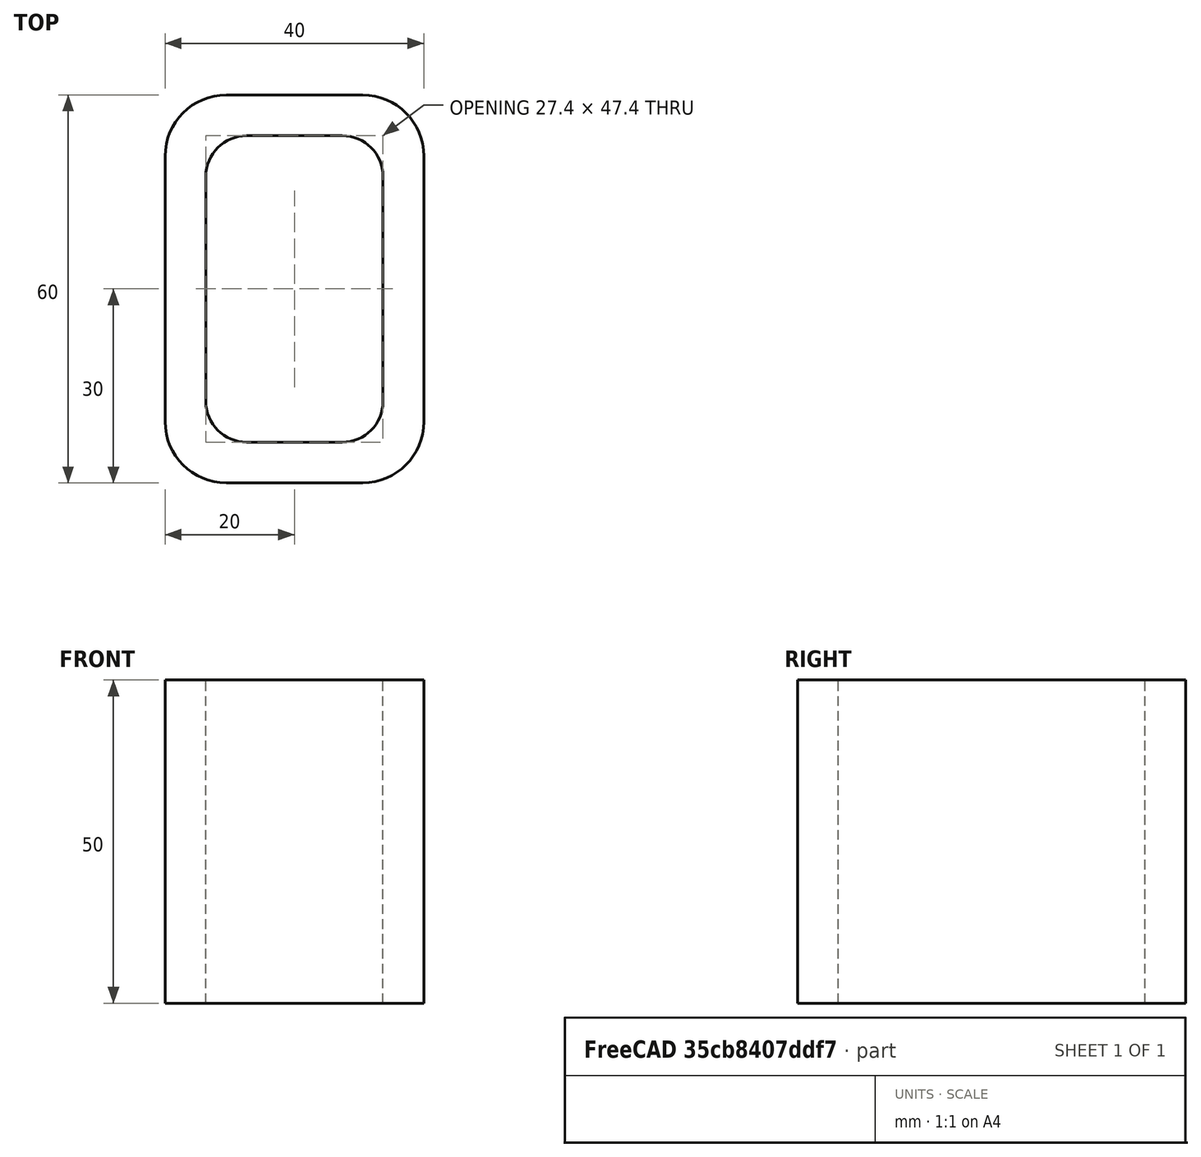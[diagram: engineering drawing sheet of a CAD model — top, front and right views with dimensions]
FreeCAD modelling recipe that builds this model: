
FCSTD DOCUMENT  (FreeCAD 0.15R4671 (Git))
Label: Rectangular hollow section 60x40x6.3 EN10219 S235JRH
License: All rights reserved
LicenseURL: http://en.wikipedia.org/wiki/All_rights_reserved
objects: Sketcher::SketchObject×1, Part::Extrusion×1
note: 2 computed .brp shape members not serialized (recipe doc carries the construction recipe); baked Part::Feature solids carry a one-line shape summary decoded from their .brp

FEATURE [Sketcher::SketchObject] Sketch
  sketch-geometry (16):
    g0: LineSegment StartX=-7.4 StartY=23.7 StartZ=0 EndX=7.4 EndY=23.7 EndZ=0
    g1: LineSegment StartX=13.7 StartY=17.4 StartZ=0 EndX=13.7 EndY=-17.4 EndZ=0
    g2: LineSegment StartX=7.4 StartY=-23.7 StartZ=0 EndX=-7.4 EndY=-23.7 EndZ=0
    g3: LineSegment StartX=-13.7 StartY=-17.4 StartZ=0 EndX=-13.7 EndY=17.4 EndZ=0
    g4: LineSegment StartX=-10.55 StartY=30 StartZ=0 EndX=10.55 EndY=30 EndZ=0
    g5: LineSegment StartX=20 StartY=20.55 StartZ=0 EndX=20 EndY=-20.55 EndZ=0
    g6: LineSegment StartX=10.55 StartY=-30 StartZ=0 EndX=-10.55 EndY=-30 EndZ=0
    g7: LineSegment StartX=-20 StartY=-20.55 StartZ=0 EndX=-20 EndY=20.55 EndZ=0
    g8: ArcOfCircle CenterX=-7.4 CenterY=17.4 CenterZ=0 NormalX=0 NormalY=0 NormalZ=1 Radius=6.3 StartAngle=1.5708 EndAngle=3.14159
    g9: ArcOfCircle CenterX=7.4 CenterY=17.4 CenterZ=0 NormalX=0 NormalY=0 NormalZ=1 Radius=6.3 StartAngle=0 EndAngle=1.5708
    g10: ArcOfCircle CenterX=7.4 CenterY=-17.4 CenterZ=0 NormalX=0 NormalY=0 NormalZ=1 Radius=6.3 StartAngle=4.71239 EndAngle=6.28319
    g11: ArcOfCircle CenterX=-7.4 CenterY=-17.4 CenterZ=0 NormalX=0 NormalY=0 NormalZ=1 Radius=6.3 StartAngle=3.14159 EndAngle=4.71239
    g12: ArcOfCircle CenterX=10.55 CenterY=20.55 CenterZ=0 NormalX=0 NormalY=0 NormalZ=1 Radius=9.45 StartAngle=0 EndAngle=1.5708
    g13: ArcOfCircle CenterX=10.55 CenterY=-20.55 CenterZ=0 NormalX=0 NormalY=0 NormalZ=1 Radius=9.45 StartAngle=4.71239 EndAngle=6.28319
    g14: ArcOfCircle CenterX=-10.55 CenterY=-20.55 CenterZ=0 NormalX=0 NormalY=0 NormalZ=1 Radius=9.45 StartAngle=3.14159 EndAngle=4.71239
    g15: ArcOfCircle CenterX=-10.55 CenterY=20.55 CenterZ=0 NormalX=0 NormalY=0 NormalZ=1 Radius=9.45 StartAngle=1.5708 EndAngle=3.14159
  constraints (36):
    c: Horizontal(g2)
    c: Vertical(g3)
    c: Horizontal(g6)
    c: Vertical(g7)
    c: Tangent(g3,g8) = 1.5708
    c: Tangent(g0,g8) = 1.5708
    c: Tangent(g0,g9) = 1.5708
    c: Tangent(g1,g9) = 1.5708
    c: Tangent(g1,g10) = 1.5708
    c: Tangent(g2,g10) = 1.5708
    c: Tangent(g2,g11) = 1.5708
    c: Tangent(g3,g11) = 1.5708
    c: Tangent(g4,g12) = 1.5708
    c: Tangent(g5,g12) = 1.5708
    c: Tangent(g5,g13) = 1.5708
    c: Tangent(g6,g13) = 1.5708
    c: Tangent(g6,g14) = 1.5708
    c: Tangent(g7,g14) = 1.5708
    c: Tangent(g7,g15) = 1.5708
    c: Tangent(g4,g15) = 1.5708
    c: Equal(g9,g8)
    c: Equal(g9,g11)
    c: Equal(g9,g10)
    c: Equal(g12,g15)
    c: Equal(g12,g14)
    c: Equal(g12,g13)
    c: Symmetric(g4,g6,g-1)
    c: Symmetric(g7,g5,g-2)
    c: DistanceY(g4,g6) = -60
    c: DistanceX(g7,g5) = 40
    c: Symmetric(g3,g1,g-2)
    c: Symmetric(g0,g2,g-1)
    c: DistanceY(g0,g4) = 6.3
    c: DistanceX(g5,g1) = -6.3
    c: Radius(g9) = 6.3
    c: Radius(g12) = 9.45
FEATURE [Part::Extrusion] Extrude  label="Rectangular hollow section 60x40x6.3 EN10219 S235JRH"
  Base = -> Sketch
  Dir = (0,0,50)
  Solid = true
